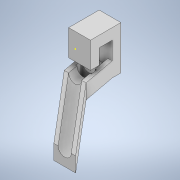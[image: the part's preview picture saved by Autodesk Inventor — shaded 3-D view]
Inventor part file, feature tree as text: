
AUTODESK INVENTOR PART (.ipt)
format: ipt  version: 2021 (Build 250183000, 183)  size: 439,808 bytes
history: native  units: mm
features: sketch x13, extrude x6, plane x3, sweep x1, thread x1, loft x1, emboss x1, other x1
ambient origin geometry x8: Origin, YZ Plane, XZ Plane, XY Plane, X Axis, Y Axis, Z Axis, Center Point
bodies: Solid1 (feature_tree)
feature tree (27):
  extrude  "Extrusion1"  Depth=50.0mm
  extrude  "Extrusion2"  Depth=12.5mm
  extrude  "Extrusion3"  Depth=3.0mm
  extrude  "Extrusion4"  Depth=6.0mm TaperAngle=0.0deg
  extrude  "Extrusion5"  Depth=15.0mm TaperAngle=0.0deg
  sketch  "Sketch6"  dims[d14=25.0mm d15=10.0mm d16=0.0mm d17=15.0mm]
  plane  "Work Plane1"
  sweep  "Sweep1"
  thread  "Thread1"  [1 undecoded]
  sketch  "Sketch9"  dims[d21=30.0mm d22=15.0mm]
  sketch  "Sketch10"  dims[d23=17.0mm]
  plane  "Work Plane2"
  extrude  "Extrusion6"  Depth=10.0mm TaperAngle=0.0deg
  sketch  "Sketch13"  dims[d25=-12.5mm]
  plane  "Work Plane3"
  loft  "Loft1"
  emboss  "Emboss1"
  sketch  "Sketch1"  dims[d0=25.0mm d1=50.0mm]
  sketch  "Sketch2"  dims[d2=12.5mm d3=12.5mm]
  sketch  "Sketch3"  dims[d4=10.0mm d5=0.0mm d7=3.0mm]
  sketch  "Sketch4"  dims[d8=33.0mm d9=6.0mm d10=0.0mm]
  sketch  "Sketch5"  dims[d11=15.0mm d12=15.0mm d13=0.0mm]
  sketch  "Sketch8"  dims[d18=15.0mm d19=10.0mm d20=0.0mm]
  sketch  "Sketch12"  dims[d24=17.0mm]
  sketch  "Sketch14"  dims[d26=2.268928mm]
  other  "Edges1"
  sketch  "Sketch15"  dims[d27=8.5mm d28=0.0mm d29=0.0mm d30=6.0mm d31=0.0mm d32=30.0mm d33=18.0mm d34=6.0mm d35=3.5mm d36=14.5mm d37=25.0mm d38=0.0mm d39=40.0mm d40=17.0mm d41=25.0mm d42=5.0mm d43=5.0mm d45=15.0mm d46=38.574mm d47=28.0mm d48=0.0mm d49=90.0deg d50=0.0mm d51=90.0deg d52=1.0mm d53=0.0mm]
note: 1 required parameter value undecoded (feature->parameter linkage not recoverable at this tier; creation-order binding heuristic only, values carry confidence <= 0.55)
